# Revit family: Door-Exterior_Interior-Simpson-Sash-Half_Glass-Single
name_source: partatom
category: Doors
revit_build: Autodesk Revit Architecture 2012 (Build: 20110916_2132(x64)
units: mm (PartAtom-declared; Revit-internal decimal feet)

## types (1)
- Door-Exterior_Interior-Simpson-Sash-Half_Glass-Single
    Arch Bottom Height = 0' - 6 15/16"
    Assembly Code = B2030230
    Bottom Panel Height = 2' - 2 3/4"
    Bottom Panel Type = Innerbond Double Hip-Raised Vertical : Vertical Panel
    Bottom Panel Width = 2' - 3 3/4"
    Bottom Rail Height = 0' - 8 13/16"
    Construction Type = Wood
    Description = Exterior French SDL - Ten Lite
    Frame = Wood - Simpson Doors - Douglas Fir
    Frame Projection Ext. = 0' - 1"
    Frame Projection Int. = 0' - 1"
    Frame Type = Frame : Standard
    Frame Width = 0' - 3"
    Full Glass = Yes
    Function = Exterior
    Glass = Glass - Simpson Doors - Clear
    Glass Options = http://simpsondoor.com
    Height = 7' - 0"
    Horizontal Outside Muntin = No
    Innerbond Double Hip-Raised Panel = Yes
    Manufacturer = Simpsons Door Company
    Middle Rail Height = 0' - 3 3/4"
    Model = 37580
    Muntin Width = 0' - 0 1/2"
    Number of Horizontal Muntins = 0
    Number of Panel Dividers = 1
    Number of Vertical Muntins = 0
    Ovolo Construction = Yes
    Panel = Wood - Simpson Doors - Douglas Fir
    Panel Divider Width = 0' - 2 1/2"
    Panel Stile Width = 0' - 4 1/8"
    Product Documentation Link = http://www.simpsondoor.com
    Product Page URL = http://www.simpsondoor.com
    Rough Height = 7' - 2"
    Rough Width = 3' - 4"
    Thickness = 0' - 1 3/4"
    Thickness Note = comes in 1 3/4" and 2 1/4" Thickness. Default is set to 1 3/4"
    Top Rail Height = 0' - 4 1/16"
    URL = http://www.simpsondoor.com
    UltraBlock Note = This Door Comes with The Option of UltraBlock Technology. It is Turn On as a Default
    UltraBlock Option = Yes
    Vertical Outside Muntin = No
    Wall Closure = By host
    WaterBarrier Note = This Door Comes with The Option of WaterBarrier with UltraBlock Technology. It is Turn Off as a Default
    WaterBarrier with UltraBlock Technology = No
    Width = 3' - 0"
    Wood Species = http://simpsondoor.com
    Wood Species Note = Available in Any Wood Species

## geometry (parser evidence)
native form markers: Blend x34, Sweep x36
no freeform markers — native parametric forms only
